# Revit family: Gira_502112
name_source: partatom
category: Elektroinstallationen
revit_build: Autodesk Revit 2017 (Build: 20160225_1515(x64)
units: mm (PartAtom-declared; Revit-internal decimal feet)

## family parameters
Basisbauteil = Fläche
Beim Laden mit Abzugskörper schneiden = Nein
Bemaßung runder Anschluss = Durchmesser verwenden
Beschriftungsausrichtung beibehalten = Nein
Gemeinsam genutzt = Nein
Raumberechnungspunkt = Nein
Teiletyp = Normal

## types (1)
- Wippenset 1f Tastsens.4 TS4 G Weiß
    Andere Bussysteme = ohne
    BIM = https://media.stage.bim.site TS4 Wippenset 1fach.rfa
    BIMSITE_PRODUCT_ID = 81f7e5b2e8a2765c84720868eaa15d83009ab7a7
    Beschreibung = Wippenset 1fach für Tastsensor 4  Glas Weiß Hinweise :  Beschreibbare Wippensets können mit einer individuellen Beschriftung versehen werden. Die Bestellung wird über den Großhandel abgewickelt, der beim Bestellvorgang der Wippen angegeben wurde.
    Bussystem Funkbus = Nein
    Bussystem KNX = Ja
    Bussystem KNX-Funk = Nein
    Bussystem LON = Nein
    Bussystem Powernet = Nein
    Datenblatt = https://media.stage.bim.site
    Datenblatt 1 = https://media.stage.bim.site
    Farbe = weiß
    Funk bidirektional = Nein
    GTIN = 4010337072058
    HAN = 502112
    HeinzeBIM = https://www.heinze.de
    Hersteller = Gira
    Kosten = 0 $
    Produktseite = https://media.stage.bim.site
    Transparent = Nein
    Typname = Wippenset 1f Tastsens.4 TS4 G Weiß
    URL = https://www.gira.de
    Vorgabe-Ansicht = 1219 mm
    Werkstoff Text = Glas

## geometry (parser evidence)
native form markers: Sweep x6
no freeform markers — native parametric forms only
